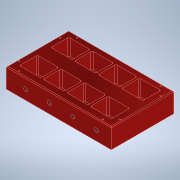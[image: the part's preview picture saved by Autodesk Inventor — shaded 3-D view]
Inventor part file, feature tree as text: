
AUTODESK INVENTOR PART (.ipt)
format: ipt  version: 2022 (Build 260153000, 153)  size: 291,328 bytes
history: native  units: mm
features: sketch x6, hole x4, projected_geometry x3, extrude x2, chamfer x1
ambient origin geometry x8: Origin, YZ Plane, XZ Plane, XY Plane, X Axis, Y Axis, Z Axis, Center Point
bodies: Volumenkörper1 (feature_tree)
feature tree (16):
  extrude  "Extrusion1"  Depth=139.7mm
  chamfer  "Fase1"  Distance=44.45mm
  sketch  "Skizze4"  dims[d11=2.0mm d12=2.0mm d13=45.0deg d153=24.0mm]
  hole  "Bohrung7"  [1 undecoded]
  extrude  "Extrusion5"  Depth=5.0mm
  hole  "Hole9"  [1 undecoded]
  hole  "Hole10"  [1 undecoded]
  hole  "Hole11"  [1 undecoded]
  sketch  "Skizze1"  dims[d0=234.95mm d2=139.7mm d3=44.45mm d4=0.0mm]
  sketch  "Sketch12"  dims[d154=24.0mm d155=5.0mm]
  projected_geometry  "Projected Loop1"
  projected_geometry  "Projected Loop2"
  projected_geometry  "Projected Loop3"
  sketch  "Sketch13"  dims[d156=5.0mm d157=24.0mm]
  sketch  "Sketch14"  dims[d158=5.0mm d159=5.0mm]
  sketch  "Sketch15"  dims[d160=24.0mm d161=24.0mm d162=5.0mm d163=5.0mm d164=24.0mm d165=5.0mm d166=24.0mm d167=5.0mm d168=24.0mm d169=3.242mm d170=6.0mm d171=8.0mm d172=4.6mm d173=14.3117mm d174=20.0mm d175=20.594885mm d193=47.75mm d194=40.0mm d195=8.5mm d196=8.5mm d197=3.0mm d198=40.0mm d200=52.75mm d201=20.0mm d203=70.0mm d206=36.0mm d207=0.0mm d209=23.0mm d210=40.0mm d212=52.75mm d213=10.0mm d215=10.0mm d217=7.95mm d218=6.924mm d219=0.624793mm d220=8.304mm d221=4.0mm d222=2.0mm d223=90.0deg d224=8.0mm d225=20.594885mm d226=40.0mm d228=52.75mm d229=10.0mm d231=10.0mm d233=7.95mm d234=6.924mm d235=0.624793mm d236=8.304mm d237=4.0mm d238=2.0mm d239=90.0deg d240=8.0mm d241=20.594885mm d242=25.4mm d243=76.2mm d244=20.0mm d246=152.4mm d247=20.0mm d249=50.8mm d252=6.756mm d253=6.924mm d254=12.878mm d255=2.0mm d256=14.3117mm d257=8.0mm d258=20.594885mm]
note: 4 required parameter values undecoded (feature->parameter linkage not recoverable at this tier; creation-order binding heuristic only, values carry confidence <= 0.55)
